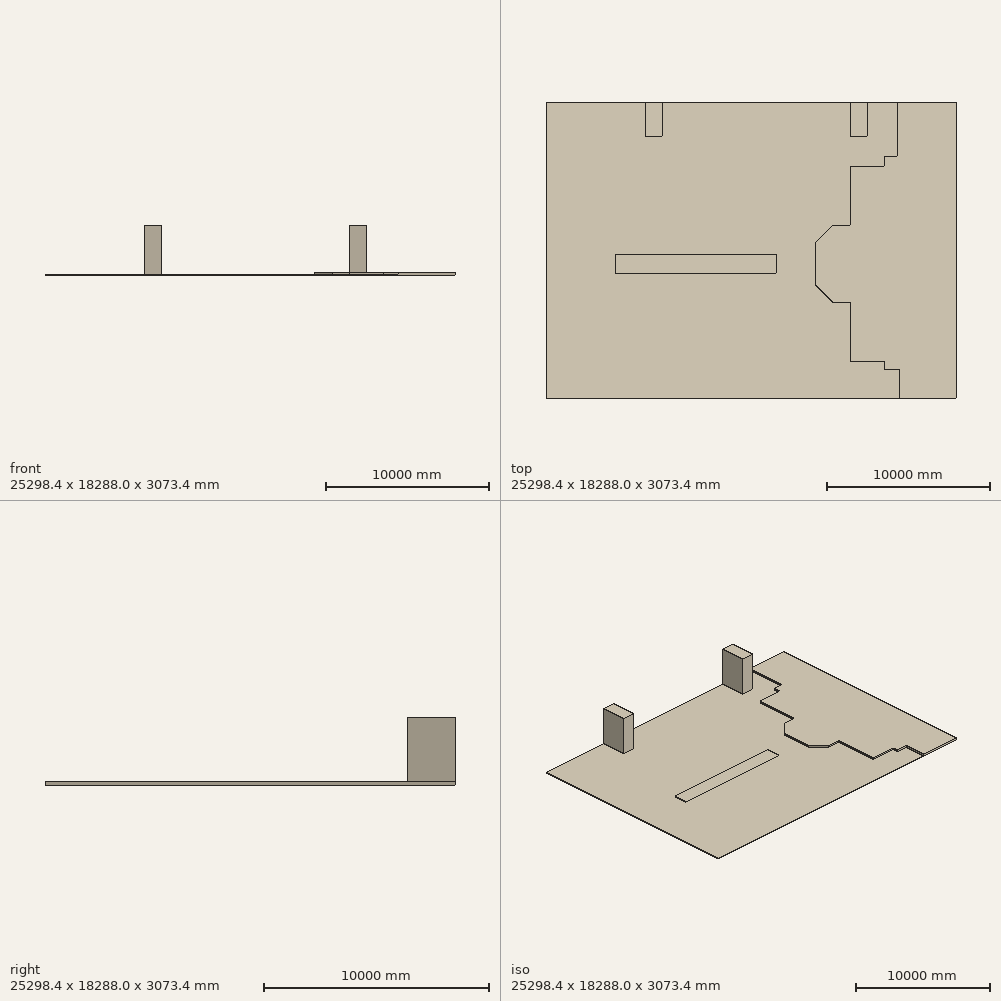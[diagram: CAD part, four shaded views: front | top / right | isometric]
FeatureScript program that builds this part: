
annotation { "Feature Type Name" : "Feature", "Feature Type Description" : "" }
export const myFeature = defineFeature(function(context is Context, id is Id, definition is map)
    precondition{}
    {
        {
            var Q0;
            Q0=qCreatedBy(makeId("Top.planeOp"),FACE);
            var sketch = newSketch(context, id + "F0", { "sketchPlane" : qUnion([Q0])});
            skLineSegment(sketch, "E0.bottom", {"start": v(0, 9144) * mm, "end": v(-25298.4, 9144) * mm});
            skLineSegment(sketch, "E0.top", {"start": v(0, -9144) * mm, "end": v(-25298.4, -9144) * mm});
            skLineSegment(sketch, "E0.left", {"start": v(0, 9144) * mm, "end": v(0, -9144) * mm});
            skLineSegment(sketch, "E0.right", {"start": v(-25298.4, 9144) * mm, "end": v(-25298.4, -9144) * mm});
            skPoint(sketch, "E0.middle", {"position": v(-12649.2, 0) * mm});
            skSolve(sketch);
        }
        {
            var Q0;
            Q0=makeQuery(id+"F0.imprint","IMPRINT",FACE,{"disambiguationData":[TD([[makeQuery(id+"F0.imprint","IMPRINT",EDGE,{"derivedFrom":sQuery(id+"F0.wireOp",EDGE,"E0.bottom")}),1.0]])]});
            extrude(context, id + "F1", {"entities" : qUnion([Q0]), "oppositeDirection" : true, "depth" : 25.4 * mm, "offsetDistance" : 25.4 * mm});
        }
        {
            var Q0;
            Q0=makeQuery(id+"F0.imprint","IMPRINT",FACE,{"disambiguationData":[TD([[makeQuery(id+"F0.imprint","IMPRINT",EDGE,{"derivedFrom":sQuery(id+"F0.wireOp",EDGE,"E0.bottom")}),1.0]])]});
            var sketch = newSketch(context, id + "F2", { "sketchPlane" : qUnion([Q0])});
            skLineSegment(sketch, "E1.bottom", {"start": v(-19202.4, 7010.4) * mm, "end": v(-18135.6, 7010.4) * mm});
            skLineSegment(sketch, "E1.top", {"start": v(-19202.4, 9144) * mm, "end": v(-18135.6, 9144) * mm});
            skLineSegment(sketch, "E1.left", {"start": v(-19202.4, 7010.4) * mm, "end": v(-19202.4, 9144) * mm});
            skLineSegment(sketch, "E1.right", {"start": v(-18135.6, 7010.4) * mm, "end": v(-18135.6, 9144) * mm});
            skLineSegment(sketch, "E2.bottom", {"start": v(-6553.2, 9144) * mm, "end": v(-5486.4, 9144) * mm});
            skLineSegment(sketch, "E2.top", {"start": v(-6553.2, 7010.4) * mm, "end": v(-5486.4, 7010.4) * mm});
            skLineSegment(sketch, "E2.left", {"start": v(-6553.2, 9144) * mm, "end": v(-6553.2, 7010.4) * mm});
            skLineSegment(sketch, "E2.right", {"start": v(-5486.4, 9144) * mm, "end": v(-5486.4, 7010.4) * mm});
            skLineSegment(sketch, "E3", {"start": v(-6553.2, 5181.6) * mm, "end": v(-6553.2, 1524) * mm});
            skLineSegment(sketch, "E4", {"start": v(-6553.2, 1524) * mm, "end": v(-7620, 1524) * mm});
            skLineSegment(sketch, "E5", {"start": v(-7620, -3200.4) * mm, "end": v(-6553.2, -3200.4) * mm});
            skLineSegment(sketch, "E6", {"start": v(-6553.2, -3200.4) * mm, "end": v(-6553.2, -6858) * mm});
            skLineSegment(sketch, "E7", {"start": v(-6553.2, -6858) * mm, "end": v(-4419.6, -6858) * mm});
            skLineSegment(sketch, "E8", {"start": v(-3505.2, -9144) * mm, "end": v(0, -9144) * mm});
            skLineSegment(sketch, "E9", {"start": v(0, -9144) * mm, "end": v(0, 9144) * mm});
            skLineSegment(sketch, "E10", {"start": v(0, 9144) * mm, "end": v(-3627.12, 9144) * mm});
            skLineSegment(sketch, "E11", {"start": v(-6553.2, 5181.6) * mm, "end": v(-4419.6, 5181.6) * mm});
            skLineSegment(sketch, "E12", {"start": v(-4419.6, 5181.6) * mm, "end": v(-4419.6, 5791.2) * mm});
            skLineSegment(sketch, "E13", {"start": v(-4419.6, -7315.2) * mm, "end": v(-4419.6, -6858) * mm});
            skLineSegment(sketch, "E14", {"start": v(-7620, 1524) * mm, "end": v(-8686.8, 457.2) * mm});
            skLineSegment(sketch, "E15", {"start": v(-8686.8, 457.2) * mm, "end": v(-8686.8, -2133.6) * mm});
            skLineSegment(sketch, "E16", {"start": v(-8686.8, -2133.6) * mm, "end": v(-7620, -3200.4) * mm});
            skLineSegment(sketch, "E17.top", {"start": v(-4419.6, 5791.2) * mm, "end": v(-3627.12, 5791.2) * mm});
            skLineSegment(sketch, "E17.right", {"start": v(-3627.12, 9144) * mm, "end": v(-3627.12, 5791.2) * mm});
            skLineSegment(sketch, "E18.top", {"start": v(-4419.6, -7315.2) * mm, "end": v(-3505.2, -7315.2) * mm});
            skLineSegment(sketch, "E18.right", {"start": v(-3505.2, -9144) * mm, "end": v(-3505.2, -7315.2) * mm});
            skPoint(sketch, "E19.orphan", {"position": v(-4419.6, 9144) * mm});
            skLineSegment(sketch, "E20", {"start": v(-8686.8, -838.2) * mm, "end": v(-21033.25, -838.2) * mm, "construction": true});
            skLineSegment(sketch, "E21", {"start": v(-11125.2, -228.6) * mm, "end": v(-21033.25, -228.6) * mm});
            skLineSegment(sketch, "E22", {"start": v(-11125.2, -1447.8) * mm, "end": v(-21033.25, -1447.8) * mm});
            skLineSegment(sketch, "E23", {"start": v(-21033.25, -1447.8) * mm, "end": v(-21033.25, -228.6) * mm});
            skLineSegment(sketch, "E24", {"start": v(-11125.2, -228.6) * mm, "end": v(-11125.2, -1447.8) * mm});
            skSolve(sketch);
        }
        {
            var Q0;
            Q0=makeQuery(id+"F2.imprint","IMPRINT",FACE,{"disambiguationData":[TD([[makeQuery(id+"F2.imprint","IMPRINT",EDGE,{"derivedFrom":sQuery(id+"F2.wireOp",EDGE,"E3")}),1.0]])]});
            var sketch = newSketch(context, id + "F3", { "sketchPlane" : qUnion([Q0])});
            skSolve(sketch);
        }
        {
            var Q0;
            Q0=makeQuery(id+"F2.imprint","IMPRINT",FACE,{"disambiguationData":[TD([[makeQuery(id+"F2.imprint","IMPRINT",EDGE,{"derivedFrom":sQuery(id+"F2.wireOp",EDGE,"E3")}),1.0]])]});
            var Q1;
            Q1 = qSketchRegion(id + "F3", true);
            extrude(context, id + "F4", {"entities" : qUnion([Q0, Q1]), "operationType" : NewBodyOperationType.ADD, "depth" : 152.4 * mm, "offsetDistance" : 30.48 * mm});
        }
        {
            var Q0;
            Q0=makeQuery(id+"F2.imprint","IMPRINT",FACE,{"disambiguationData":[TD([[makeQuery(id+"F2.imprint","IMPRINT",EDGE,{"derivedFrom":sQuery(id+"F2.wireOp",EDGE,"E1.bottom")}),1.0]])]});
            var Q1;
            Q1=makeQuery(id+"F2.imprint","IMPRINT",FACE,{"disambiguationData":[TD([[makeQuery(id+"F2.imprint","IMPRINT",EDGE,{"derivedFrom":sQuery(id+"F2.wireOp",EDGE,"E2.bottom")}),1.0]])]});
            extrude(context, id + "F5", {"entities" : qUnion([Q0, Q1]), "operationType" : NewBodyOperationType.ADD, "depth" : 3048 * mm, "offsetDistance" : 30.48 * mm});
        }
        {
            var Q0;
            {var subQ0=sQuery(id+"F2.wireOp",EDGE,"E21");Q0=makeQuery(id+"F2.imprint","IMPRINT",FACE,{"disambiguationData":[TD([[makeQuery(id+"F2.imprint","IMPRINT",EDGE,{"derivedFrom":subQ0}),1.0]])]});}
            extrude(context, id + "F6", {"entities" : qUnion([Q0]), "operationType" : NewBodyOperationType.ADD, "depth" : 25.4 * mm, "offsetDistance" : 30.48 * mm});
        }
    });
